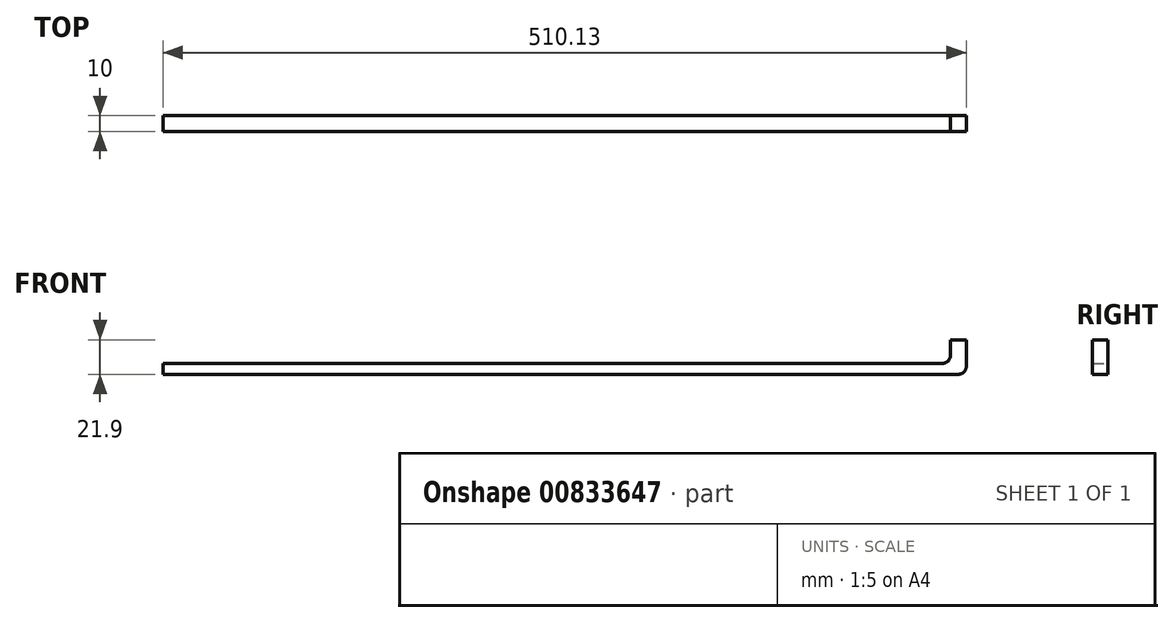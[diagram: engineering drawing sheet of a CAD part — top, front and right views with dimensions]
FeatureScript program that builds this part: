
annotation { "Feature Type Name" : "Feature", "Feature Type Description" : "" }
export const myFeature = defineFeature(function(context is Context, id is Id, definition is map)
    precondition{}
    {
        {
            var Q0;
            Q0=qCreatedBy(makeId("Front.planeOp"),FACE);
            var sketch = newSketch(context, id + "F0", { "sketchPlane" : qUnion([Q0])});
            skLineSegment(sketch, "E0.bottom", {"start": v(-49.57, 32.46) * mm, "end": v(-42.35, 32.46) * mm});
            skLineSegment(sketch, "E0.top", {"start": v(-49.57, -30.69) * mm, "end": v(-42.35, -30.69) * mm});
            skLineSegment(sketch, "E0.left", {"start": v(-49.57, 32.46) * mm, "end": v(-49.57, -30.69) * mm});
            skLineSegment(sketch, "E0.right", {"start": v(-42.35, 32.46) * mm, "end": v(-42.35, -30.69) * mm});
            skLineSegment(sketch, "E1.bottom", {"start": v(457.65, 25.98) * mm, "end": v(467.65, 25.98) * mm});
            skLineSegment(sketch, "E1.top", {"start": v(457.65, 15.98) * mm, "end": v(467.65, 15.98) * mm});
            skLineSegment(sketch, "E1.left", {"start": v(457.65, 25.98) * mm, "end": v(457.65, 15.98) * mm});
            skLineSegment(sketch, "E1.right", {"start": v(467.65, 25.98) * mm, "end": v(467.65, 15.98) * mm});
            skLineSegment(sketch, "E2.bottom", {"start": v(7.62, 34.53) * mm, "end": v(31.88, 34.53) * mm});
            skLineSegment(sketch, "E2.top", {"start": v(7.62, 27.91) * mm, "end": v(31.88, 27.91) * mm});
            skLineSegment(sketch, "E2.left", {"start": v(7.62, 34.53) * mm, "end": v(7.62, 27.91) * mm});
            skLineSegment(sketch, "E2.right", {"start": v(31.88, 34.53) * mm, "end": v(31.88, 27.91) * mm});
            skSolve(sketch);
        }
        {
            var Q0;
            Q0 = qSketchRegion(id + "F0", true);
            extrude(context, id + "F1", {"entities" : qUnion([Q0]), "depth" : 25 * mm, "offsetDistance" : 25 * mm});
        }
        {
            var Q0;
            Q0=makeQuery(id+"F1.opExtrude","SWEPT_BODY",BODY,{"disambiguationData":[OSD([sQuery(id+"F0.wireOp",EDGE,"E2.bottom"),sQuery(id+"F0.wireOp",EDGE,"E2.top"),sQuery(id+"F0.wireOp",EDGE,"E2.left"),sQuery(id+"F0.wireOp",EDGE,"E2.right")])]});
            deleteBodies(context, id + "F2", {"entities" : qUnion([Q0])});
        }
        {
            var Q0;
            Q0=qCreatedBy(makeId("Front.planeOp"),FACE);
            var sketch = newSketch(context, id + "F3", { "sketchPlane" : qUnion([Q0])});
            skLineSegment(sketch, "E3.bottom", {"start": v(-47.8, 0) * mm, "end": v(467.78, 0) * mm});
            skLineSegment(sketch, "E3.top", {"start": v(-47.8, -7) * mm, "end": v(467.78, -7) * mm});
            skLineSegment(sketch, "E3.left", {"start": v(-47.8, 0) * mm, "end": v(-47.8, -7) * mm});
            skLineSegment(sketch, "E3.right", {"start": v(467.78, 0) * mm, "end": v(467.78, -7) * mm});
            skLineSegment(sketch, "E4.bottom", {"start": v(467.78, 0) * mm, "end": v(457.78, 0) * mm});
            skLineSegment(sketch, "E4.top", {"start": v(467.78, 14.9) * mm, "end": v(457.78, 14.9) * mm});
            skLineSegment(sketch, "E4.left", {"start": v(467.78, 0) * mm, "end": v(467.78, 14.9) * mm});
            skLineSegment(sketch, "E4.right", {"start": v(457.78, 0) * mm, "end": v(457.78, 14.9) * mm});
            skSolve(sketch);
        }
        {
            var Q0;
            Q0 = qSketchRegion(id + "F3", true);
            extrude(context, id + "F4", {"entities" : qUnion([Q0]), "operationType" : NewBodyOperationType.ADD, "depth" : 10 * mm, "offsetDistance" : 25 * mm});
        }
        {
            var Q0;
            Q0=makeQuery(id+"F4.opExtrude","SWEPT_EDGE",EDGE,{"disambiguationData":[OSD([sQuery(id+"F3.wireOp",EDGE,"E3.bottom"),sQuery(id+"F3.wireOp",EDGE,"E4.bottom"),sQuery(id+"F3.wireOp",EDGE,"E4.right")])]});
            var Q1;
            Q1=makeQuery(id+"F4.opExtrude","SWEPT_EDGE",EDGE,{"disambiguationData":[OSD([sQuery(id+"F3.wireOp",EDGE,"E3.top"),sQuery(id+"F3.wireOp",EDGE,"E3.right")])]});
            fillet(context, id + "F5", {"entities" : qUnion([Q0, Q1]), "radius" : 5 * mm, "tangentPropagation" : true, "allowEdgeOverflow" : false});
        }
        {
            var Q0;
            Q0=makeQuery(id+"F1.opExtrude","CAP_FACE",FACE,{"disambiguationData":[OSD([sQuery(id+"F0.wireOp",EDGE,"E0.bottom"),sQuery(id+"F0.wireOp",EDGE,"E0.top"),sQuery(id+"F0.wireOp",EDGE,"E0.left"),sQuery(id+"F0.wireOp",EDGE,"E0.right")])],"isStart":false});
            extrude(context, id + "F6", {"entities" : qUnion([Q0]), "operationType" : NewBodyOperationType.REMOVE, "oppositeDirection" : true, "depth" : 25 * mm, "offsetDistance" : 25 * mm});
        }
        {
            var Q0;
            Q0=makeQuery(id+"F1.opExtrude","SWEPT_BODY",BODY,{"disambiguationData":[OSD([sQuery(id+"F0.wireOp",EDGE,"E1.bottom"),sQuery(id+"F0.wireOp",EDGE,"E1.top"),sQuery(id+"F0.wireOp",EDGE,"E1.left"),sQuery(id+"F0.wireOp",EDGE,"E1.right")])]});
            deleteBodies(context, id + "F7", {"entities" : qUnion([Q0])});
        }
    });
